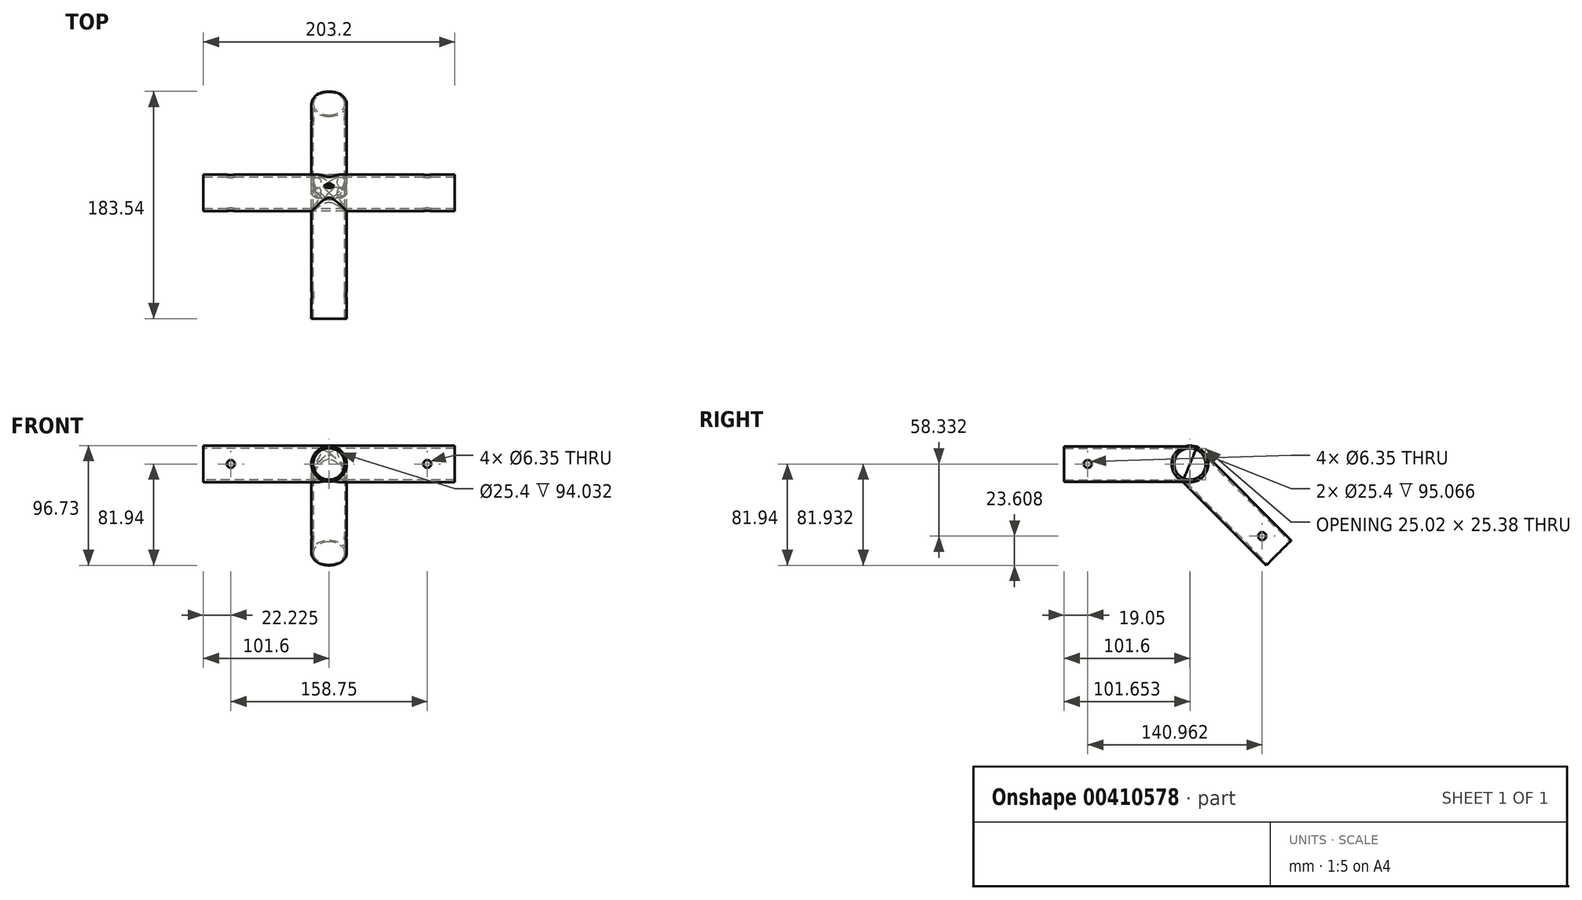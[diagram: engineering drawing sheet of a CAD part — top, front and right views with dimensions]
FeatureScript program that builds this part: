
annotation { "Feature Type Name" : "Feature", "Feature Type Description" : "" }
export const myFeature = defineFeature(function(context is Context, id is Id, definition is map)
    precondition{}
    {
        {
            var Q0;
            Q0=qCreatedBy(makeId("Front.planeOp"),FACE);
            var sketch = newSketch(context, id + "F0", { "sketchPlane" : qUnion([Q0])});
            skCircle(sketch, "E0", {"center": v(0, 0) * mm, "radius": 12.7 * mm});
            skCircle(sketch, "E1.0", {"center": v(0, 0) * mm, "radius": 14.29 * mm});
            skSolve(sketch);
        }
        {
            var Q0;
            Q0=qCreatedBy(makeId("Right.planeOp"),FACE);
            var sketch = newSketch(context, id + "F1", { "sketchPlane" : qUnion([Q0])});
            skLineSegment(sketch, "E2", {"start": v(101.6, 0) * mm, "end": v(173.44, -71.84) * mm});
            skLineSegment(sketch, "E3", {"start": v(101.6, 0) * mm, "end": v(0, 0) * mm});
            skSolve(sketch);
        }
        {
            var Q0;
            Q0=qSketchRegion(id+"F0",true);
            var Q1;
            Q1=sQuery(id+"F1.wireOp",EDGE,"E3");
            var Q2;
            Q2=sQuery(id+"F1.wireOp",EDGE,"E2");
            sweep(context, id + "F2", {"profiles" : qUnion([Q0]), "path" : qUnion([Q1, Q2])});
        }
        {
            var Q0;
            Q0=qCreatedBy(makeId("Right.planeOp"),FACE);
            var sketch = newSketch(context, id + "F3", { "sketchPlane" : qUnion([Q0])});
            skCircle(sketch, "E4", {"center": v(19.05, 0) * mm, "radius": 3.18 * mm});
            skSolve(sketch);
        }
        {
            var Q0;
            Q0=qSketchRegion(id+"F3",true);
            extrude(context, id + "F4", {"entities" : qUnion([Q0]), "operationType" : NewBodyOperationType.REMOVE, "endBound" : BoundingType.THROUGH_ALL, "oppositeDirection" : true, "depth" : 25.4 * mm, "hasSecondDirection" : true, "secondDirectionOppositeDirection" : false, "secondDirectionDepth" : 25.4 * mm});
        }
        {
            var Q0;
            Q0=qCreatedBy(makeId("Right.planeOp"),FACE);
            var sketch = newSketch(context, id + "F5", { "sketchPlane" : qUnion([Q0])});
            skCircle(sketch, "E5", {"center": v(160.01, -58.33) * mm, "radius": 3.18 * mm});
            skSolve(sketch);
        }
        {
            var Q0;
            Q0=qSketchRegion(id+"F5",true);
            extrude(context, id + "F6", {"entities" : qUnion([Q0]), "operationType" : NewBodyOperationType.REMOVE, "endBound" : BoundingType.THROUGH_ALL, "oppositeDirection" : true, "depth" : 25.4 * mm, "hasSecondDirection" : true, "secondDirectionOppositeDirection" : false, "secondDirectionDepth" : 25.4 * mm});
        }
        {
            var Q0;
            Q0=qCreatedBy(makeId("Right.planeOp"),FACE);
            var sketch = newSketch(context, id + "F7", { "sketchPlane" : qUnion([Q0])});
            skCircle(sketch, "E6", {"center": v(101.6, 0) * mm, "radius": 12.7 * mm});
            skCircle(sketch, "E7", {"center": v(101.6, 0) * mm, "radius": 14.79 * mm});
            skSolve(sketch);
        }
        {
            var Q0;
            Q0=qSketchRegion(id+"F7",true);
            extrude(context, id + "F8", {"entities" : qUnion([Q0]), "operationType" : NewBodyOperationType.ADD, "endBound" : BoundingType.SYMMETRIC, "depth" : 203.2 * mm});
        }
        {
            var Q0;
            Q0=qCreatedBy(makeId("Front.planeOp"),FACE);
            var sketch = newSketch(context, id + "F9", { "sketchPlane" : qUnion([Q0])});
            skCircle(sketch, "E8", {"center": v(79.38, 0) * mm, "radius": 3.18 * mm});
            skCircle(sketch, "E9", {"center": v(-79.38, 0) * mm, "radius": 3.18 * mm});
            skSolve(sketch);
        }
        {
            var Q0;
            Q0=qSketchRegion(id+"F9",true);
            extrude(context, id + "F10", {"entities" : qUnion([Q0]), "operationType" : NewBodyOperationType.REMOVE, "endBound" : BoundingType.THROUGH_ALL, "oppositeDirection" : true, "depth" : 25.4 * mm});
        }
    });
